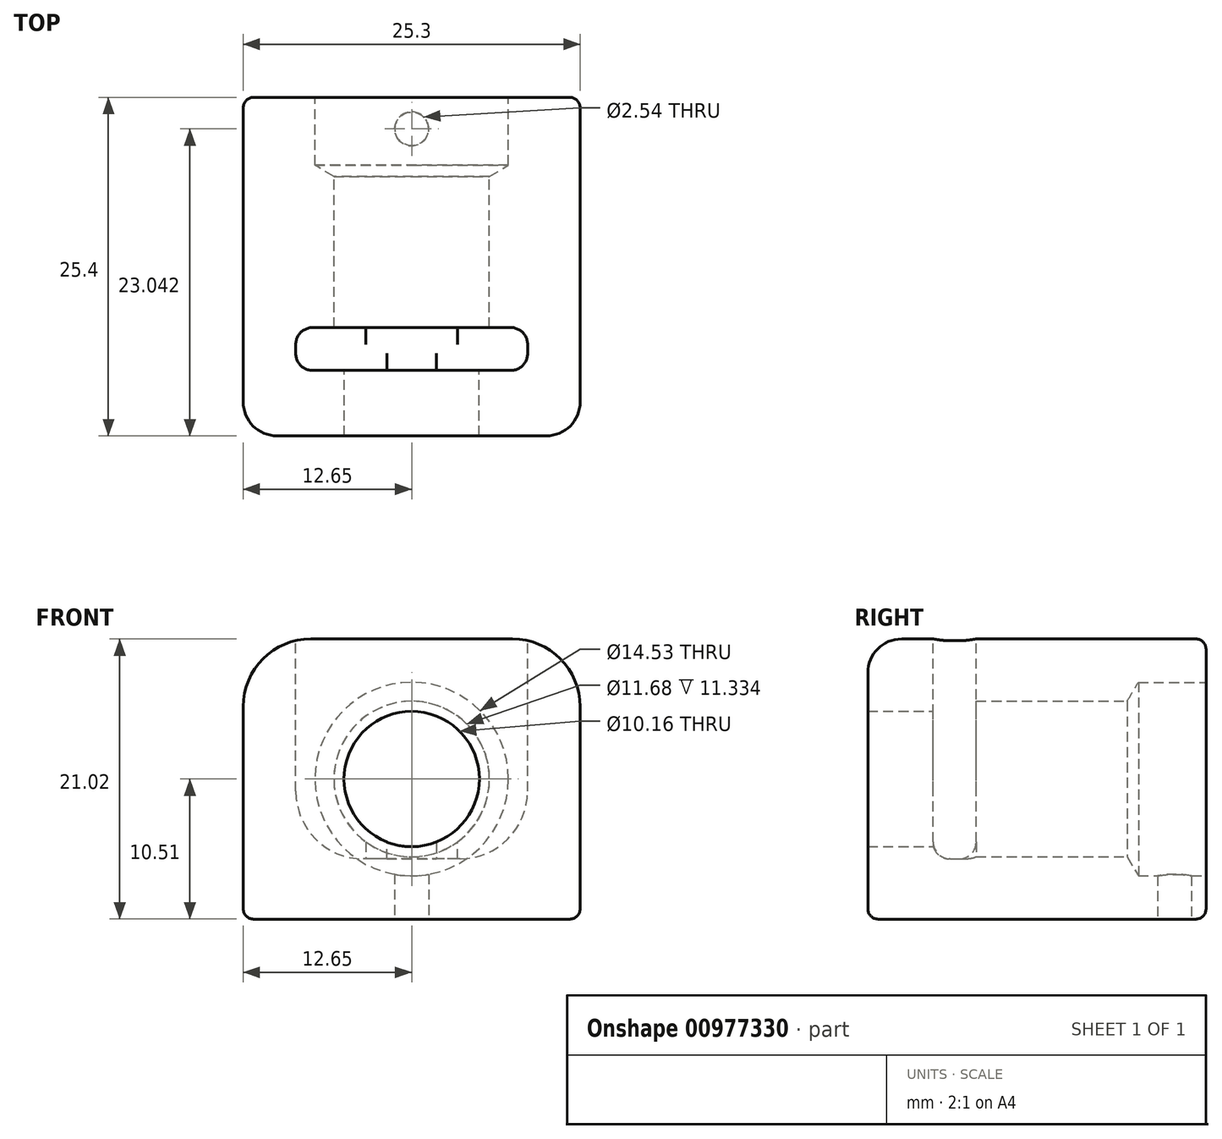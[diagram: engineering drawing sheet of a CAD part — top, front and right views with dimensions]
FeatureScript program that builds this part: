
annotation { "Feature Type Name" : "Feature", "Feature Type Description" : "" }
export const myFeature = defineFeature(function(context is Context, id is Id, definition is map)
    precondition{}
    {
        {
            var Q0;
            Q0=qCreatedBy(makeId("Front.planeOp"),FACE);
            var sketch = newSketch(context, id + "F0", { "sketchPlane" : qUnion([Q0])});
            skLineSegment(sketch, "E0.bottom", {"start": v(12.65, -10.51) * mm, "end": v(-12.65, -10.51) * mm});
            skLineSegment(sketch, "E0.top", {"start": v(12.65, 10.51) * mm, "end": v(-12.65, 10.51) * mm});
            skLineSegment(sketch, "E0.left", {"start": v(12.65, -10.51) * mm, "end": v(12.65, 10.51) * mm});
            skLineSegment(sketch, "E0.right", {"start": v(-12.65, -10.51) * mm, "end": v(-12.65, 10.51) * mm});
            skPoint(sketch, "E0.middle", {"position": v(0, 0) * mm});
            skSolve(sketch);
        }
        {
            var Q0;
            Q0=makeQuery(id+"F0.imprint","IMPRINT",FACE,{"disambiguationData":[TD([[makeQuery(id+"F0.imprint","IMPRINT",EDGE,{"derivedFrom":sQuery(id+"F0.wireOp",EDGE,"E0.bottom")}),-1.0]])]});
            extrude(context, id + "F1", {"entities" : qUnion([Q0]), "depth" : 25.4 * mm, "offsetDistance" : 25.4 * mm});
        }
        {
            var Q0;
            Q0=makeQuery(id+"F1.opExtrude","CAP_FACE",FACE,{"disambiguationData":[OSD([sQuery(id+"F0.wireOp",EDGE,"E0.bottom"),sQuery(id+"F0.wireOp",EDGE,"E0.top"),sQuery(id+"F0.wireOp",EDGE,"E0.left"),sQuery(id+"F0.wireOp",EDGE,"E0.right")])],"isStart":true});
            var sketch = newSketch(context, id + "F2", { "sketchPlane" : qUnion([Q0])});
            skCircle(sketch, "E1", {"center": v(0, 0) * mm, "radius": 5.08 * mm});
            skSolve(sketch);
        }
        {
            var Q0;
            Q0=sQuery(id+"F2.wireOp",VERTEX,"E1.center");
            var Q1;
            Q1=makeQuery(id+"F1.opExtrude","SWEPT_BODY",BODY,{"disambiguationData":[OSD([sQuery(id+"F0.wireOp",EDGE,"E0.bottom"),sQuery(id+"F0.wireOp",EDGE,"E0.top"),sQuery(id+"F0.wireOp",EDGE,"E0.left"),sQuery(id+"F0.wireOp",EDGE,"E0.right")])]});
            hole(context, id + "F3", {"style" : HoleStyle.C_BORE, "endStyle" : HoleEndStyle.THROUGH, "holeDiameter" : 10.16 * mm, "cBoreDiameter" : 11.68 * mm, "cBoreDepth" : 20.32 * mm, "majorDiameter" : 6.35 * mm, "isTappedThrough" : true, "tappedDepth" : 12.7 * mm, "tapClearance" : 3, "startFromSketch" : true, "locations" : qUnion([Q0]), "scope" : qUnion([Q1])});
        }
        {
            var Q0;
            Q0=makeQuery(id+"F1.opExtrude","CAP_FACE",FACE,{"disambiguationData":[OSD([sQuery(id+"F0.wireOp",EDGE,"E0.bottom"),sQuery(id+"F0.wireOp",EDGE,"E0.top"),sQuery(id+"F0.wireOp",EDGE,"E0.left"),sQuery(id+"F0.wireOp",EDGE,"E0.right")])],"isStart":true});
            var sketch = newSketch(context, id + "F4", { "sketchPlane" : qUnion([Q0])});
            skCircle(sketch, "E2", {"center": v(0, 0) * mm, "radius": 5.97 * mm});
            skSolve(sketch);
        }
        {
            var Q0;
            Q0=makeQuery(id+"F1.opExtrude","SWEPT_FACE",FACE,{"disambiguationData":[OSD([sQuery(id+"F0.wireOp",EDGE,"E0.top")])]});
            var sketch = newSketch(context, id + "F5", { "sketchPlane" : qUnion([Q0])});
            skLineSegment(sketch, "E3.bottom", {"start": v(8.7, -20.5) * mm, "end": v(-8.7, -20.5) * mm});
            skLineSegment(sketch, "E3.top", {"start": v(8.7, -17.27) * mm, "end": v(-8.7, -17.27) * mm});
            skLineSegment(sketch, "E3.left", {"start": v(8.7, -20.5) * mm, "end": v(8.7, -17.27) * mm});
            skLineSegment(sketch, "E3.right", {"start": v(-8.7, -20.5) * mm, "end": v(-8.7, -17.27) * mm});
            skPoint(sketch, "E3.middle", {"position": v(0, -18.88) * mm});
            skSolve(sketch);
        }
        {
            var Q0;
            Q0=makeQuery(id+"F5.imprint","IMPRINT",FACE,{"disambiguationData":[TD([[makeQuery(id+"F5.imprint","IMPRINT",EDGE,{"derivedFrom":sQuery(id+"F5.wireOp",EDGE,"E3.bottom")}),-1.0]])]});
            extrude(context, id + "F6", {"entities" : qUnion([Q0]), "operationType" : NewBodyOperationType.REMOVE, "oppositeDirection" : true, "depth" : 16.5 * mm, "offsetDistance" : 25.4 * mm});
        }
        {
            var Q0;
            Q0=makeQuery(id+"F6.boolean.opBoolean","COPY",EDGE,{"derivedFrom":makeQuery(id+"F6.opExtrude","CAP_EDGE",EDGE,{"disambiguationData":[OSD([sQuery(id+"F5.wireOp",EDGE,"E3.right")])],"isStart":false})});
            var Q1;
            Q1=makeQuery(id+"F6.boolean.opBoolean","COPY",EDGE,{"derivedFrom":makeQuery(id+"F6.opExtrude","CAP_EDGE",EDGE,{"disambiguationData":[OSD([sQuery(id+"F5.wireOp",EDGE,"E3.left")])],"isStart":false})});
            var Q2;
            Q2=makeQuery(id+"F1.opExtrude","SWEPT_EDGE",EDGE,{"disambiguationData":[OSD([sQuery(id+"F0.wireOp",EDGE,"E0.top"),sQuery(id+"F0.wireOp",EDGE,"E0.left")])]});
            var Q3;
            Q3=makeQuery(id+"F1.opExtrude","SWEPT_EDGE",EDGE,{"disambiguationData":[OSD([sQuery(id+"F0.wireOp",EDGE,"E0.top"),sQuery(id+"F0.wireOp",EDGE,"E0.right")])]});
            fillet(context, id + "F7", {"entities" : qUnion([Q0, Q1, Q2, Q3]), "radius" : 5.08 * mm, "tangentPropagation" : true, "allowEdgeOverflow" : false});
        }
        {
            var Q0;
            Q0=makeQuery(id+"F1.opExtrude","CAP_EDGE",EDGE,{"disambiguationData":[OSD([sQuery(id+"F0.wireOp",EDGE,"E0.top")])],"isStart":false});
            fillet(context, id + "F8", {"entities" : qUnion([Q0]), "radius" : 2.54 * mm, "tangentPropagation" : true, "allowEdgeOverflow" : false});
        }
        {
            var Q0;
            Q0=makeQuery(id+"F1.opExtrude","CAP_EDGE",EDGE,{"disambiguationData":[OSD([sQuery(id+"F0.wireOp",EDGE,"E0.bottom")])],"isStart":false});
            var Q1;
            Q1=makeQuery(id+"F1.opExtrude","CAP_EDGE",EDGE,{"disambiguationData":[OSD([sQuery(id+"F0.wireOp",EDGE,"E0.top")])],"isStart":true});
            var Q2;
            Q2=makeQuery(id+"F1.opExtrude","CAP_EDGE",EDGE,{"disambiguationData":[OSD([sQuery(id+"F0.wireOp",EDGE,"E0.bottom")])],"isStart":true});
            fillet(context, id + "F9", {"entities" : qUnion([Q0, Q1, Q2]), "radius" : 0.76 * mm, "tangentPropagation" : true, "allowEdgeOverflow" : false});
        }
        {
            var Q0;
            Q0=makeQuery(id+"F6.boolean.opBoolean","COPY",EDGE,{"derivedFrom":makeQuery(id+"F6.opExtrude","SWEPT_EDGE",EDGE,{"disambiguationData":[OSD([sQuery(id+"F5.wireOp",EDGE,"E3.bottom"),sQuery(id+"F5.wireOp",EDGE,"E3.left")])]})});
            var Q1;
            Q1=makeQuery(id+"F6.boolean.opBoolean","COPY",EDGE,{"derivedFrom":makeQuery(id+"F6.opExtrude","SWEPT_EDGE",EDGE,{"disambiguationData":[OSD([sQuery(id+"F5.wireOp",EDGE,"E3.top"),sQuery(id+"F5.wireOp",EDGE,"E3.left")])]})});
            var Q2;
            Q2=makeQuery(id+"F3.hole-0.boolean.opBoolean","INTERSECT",EDGE,{"derivedFrom":[makeQuery(id+"F1.opExtrude","CAP_FACE",FACE,{"disambiguationData":[OSD([sQuery(id+"F0.wireOp",EDGE,"E0.bottom"),sQuery(id+"F0.wireOp",EDGE,"E0.top"),sQuery(id+"F0.wireOp",EDGE,"E0.left"),sQuery(id+"F0.wireOp",EDGE,"E0.right")])],"isStart":false}),makeQuery(id+"F3.hole-0.opRevolve","SWEPT_FACE",FACE,{"disambiguationData":[OSD([sQuery(id+"F3.hole-0.sketch.wireOp",EDGE,"core_line_2")])]})]});
            fillet(context, id + "F10", {"entities" : qUnion([Q0, Q1, Q2]), "radius" : 1.27 * mm, "tangentPropagation" : true, "allowEdgeOverflow" : false});
        }
        {
            var Q0;
            Q0=sQuery(id+"F4.wireOp",VERTEX,"E2.center");
            var Q1;
            Q1=makeQuery(id+"F1.opExtrude","SWEPT_BODY",BODY,{"disambiguationData":[OSD([sQuery(id+"F0.wireOp",EDGE,"E0.bottom"),sQuery(id+"F0.wireOp",EDGE,"E0.top"),sQuery(id+"F0.wireOp",EDGE,"E0.left"),sQuery(id+"F0.wireOp",EDGE,"E0.right")])]});
            hole(context, id + "F11", {"style" : HoleStyle.SIMPLE, "endStyle" : HoleEndStyle.BLIND, "holeDiameter" : 14.53 * mm, "majorDiameter" : 6.35 * mm, "holeDepth" : 5.08 * mm, "isTappedThrough" : true, "tappedDepth" : 12.7 * mm, "tapClearance" : 3, "startFromSketch" : true, "locations" : qUnion([Q0]), "scope" : qUnion([Q1])});
        }
        {
            var Q0;
            Q0=makeQuery(id+"F1.opExtrude","SWEPT_FACE",FACE,{"disambiguationData":[OSD([sQuery(id+"F0.wireOp",EDGE,"E0.bottom")])]});
            var sketch = newSketch(context, id + "F12", { "sketchPlane" : qUnion([Q0])});
            skCircle(sketch, "E4", {"center": v(0, 2.36) * mm, "radius": 1.14 * mm});
            skSolve(sketch);
        }
        {
            var Q0;
            Q0=sQuery(id+"F12.wireOp",VERTEX,"E4.center");
            var Q1;
            Q1=makeQuery(id+"F1.opExtrude","SWEPT_BODY",BODY,{"disambiguationData":[OSD([sQuery(id+"F0.wireOp",EDGE,"E0.bottom"),sQuery(id+"F0.wireOp",EDGE,"E0.top"),sQuery(id+"F0.wireOp",EDGE,"E0.left"),sQuery(id+"F0.wireOp",EDGE,"E0.right")])]});
            hole(context, id + "F13", {"style" : HoleStyle.SIMPLE, "endStyle" : HoleEndStyle.BLIND, "holeDiameter" : 2.54 * mm, "majorDiameter" : 6.35 * mm, "holeDepth" : 5.08 * mm, "isTappedThrough" : true, "tappedDepth" : 12.7 * mm, "tapClearance" : 3, "startFromSketch" : true, "locations" : qUnion([Q0]), "scope" : qUnion([Q1])});
        }
    });
